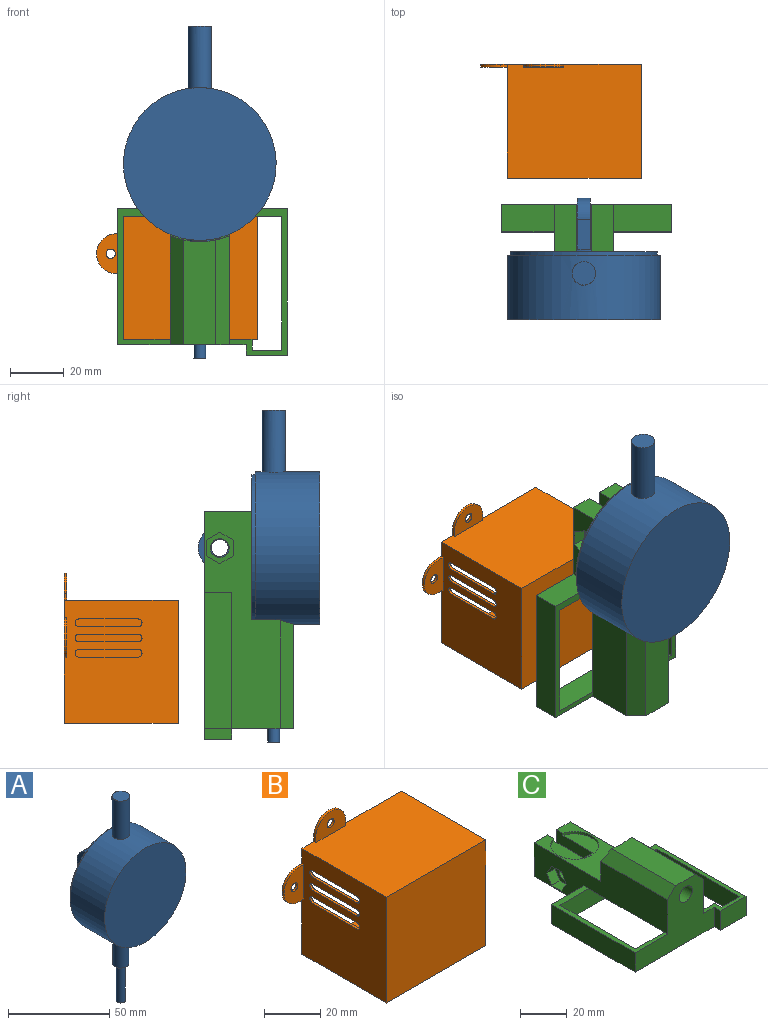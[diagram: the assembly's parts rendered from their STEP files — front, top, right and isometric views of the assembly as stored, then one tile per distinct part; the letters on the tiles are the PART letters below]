
ASSEMBLY  parts=3 mates=2
PART A: 31 faces, bbox 57x45.3x123.9 mm
  f0: cylinder r=28.5mm len=57mm, axis (0,1,0), area 4187.4mm2, adj f11,f12,f13,f15
  f1: plane 19x15.8mm, normal (1,0,0), area 242.2mm2, adj f3,f5,f6,f7,f8
  f2: plane 19x15.8mm, normal (-1,0,0), area 242.2mm2, adj f3,f5,f6,f7,f8
  f3: plane 20x20mm, normal (0,1,0), area 235.2mm2, adj f1,f2,f4,f5,f6
  f4: cylinder r=10mm len=20mm, axis (0,-1,0), area 62.8mm2, adj f3,f10
  f5: plane 11.1x5mm, normal (0,0,-1), area 55.5mm2, adj f1,f2,f3,f7
  f6: plane 11.1x5mm, normal (0,0,1), area 55.5mm2, adj f1,f2,f3,f7
  f7: cylinder r=7.9mm len=15.8mm, axis (1,0,0), area 124.1mm2, adj f1,f2,f5,f6
  f8: cylinder r=3.15mm len=6.3mm, axis (1,0,0), area 99mm2, adj f1,f2
  f9: cylinder r=27.4mm len=54.8mm, axis (0,1,0), area 223.8mm2, adj f10,f12
  f10: plane 54.8x54.8mm, normal (0,1,0), area 1980.8mm2, adj f4,f9,f21,f24,f27,f30
  f11: plane 57x57mm, normal (0,-1,0), area 2551.8mm2, adj f0
  f12: plane 57x57mm, normal (0,1,0), area 193.2mm2, adj f0,f9
  f13: cylinder r=4.35mm len=23.33mm, axis (0,0,-1), area 633.2mm2, adj f0,f14
  f14: plane 8.7x8.7mm, normal (0,0,1), area 59.4mm2, adj f13
  f15: cylinder r=4mm len=21.78mm, axis (0,0,1), area 543.9mm2, adj f0,f16
  f16: plane 8x8mm, normal (0,0,-1), area 35.1mm2, adj f15,f17
  f17: cylinder r=2.2mm len=22.4mm, axis (0,0,1), area 309.6mm2, adj f16,f18
  f18: plane 4.4x4.4mm, normal (0,0,-1), area 15.2mm2, adj f17
  f19: cone r=0mm half-angle=59deg, axis (0,1,0), area 3.7mm2, adj f20
  f20: cylinder r=1mm len=2mm, axis (0,1,0), area 4.7mm2, adj f19,f21
  f21: cone r=1mm half-angle=45deg, axis (0,1,0), area 18mm2, adj f10,f20
  f22: cone r=0mm half-angle=59deg, axis (0,1,0), area 3.7mm2, adj f23
  f23: cylinder r=1mm len=2mm, axis (0,1,0), area 4.7mm2, adj f22,f24
  f24: cone r=1mm half-angle=45deg, axis (0,1,0), area 18mm2, adj f10,f23
  f25: cone r=0mm half-angle=59deg, axis (0,1,0), area 3.7mm2, adj f26
  f26: cylinder r=1mm len=2mm, axis (0,1,0), area 4.7mm2, adj f25,f27
  f27: cone r=1mm half-angle=45deg, axis (0,1,0), area 18mm2, adj f10,f26
  f28: cone r=0mm half-angle=59deg, axis (0,1,0), area 3.7mm2, adj f29
  f29: cylinder r=1mm len=2mm, axis (0,1,0), area 4.7mm2, adj f28,f30
  f30: cone r=1mm half-angle=45deg, axis (0,1,0), area 18mm2, adj f10,f29
PART B: 33 faces, bbox 60x42.5x56 mm
  f0: plane 46x42.5mm, normal (-1,0,0), area 1735mm2, adj f1,f3,f4,f5,f11,f12,f15,f21
  f1: plane 50x42.5mm, normal (0,0,-1), area 2125mm2, adj f0,f2,f4,f5
  f2: plane 46x42.5mm, normal (1,0,0), area 1955mm2, adj f1,f3,f4,f5
  f3: plane 50x42.5mm, normal (0,0,1), area 2110mm2, adj f0,f2,f4,f5,f7,f9,f10
  f4: plane 50x46mm, normal (0,-1,0), area 2300mm2, adj f0,f1,f2,f3
  f5: plane 60x56mm, normal (0,1,0), area 420.5mm2, adj f0,f1,f2,f3,f6,f7,f8,f9
  f6: cylinder r=7.5mm len=15mm, axis (0,1,0), area 23.6mm2, adj f5,f7,f9,f10
  f7: plane 2.5x1mm, normal (-1,0,0), area 2.5mm2, adj f3,f5,f6,f10
  f8: cylinder r=1.75mm len=3.5mm, axis (0,1,0), area 11mm2, adj f5,f10
  f9: plane 2.5x1mm, normal (1,0,0), area 2.5mm2, adj f3,f5,f6,f10
  f10: plane 15x10mm, normal (0,-1,0), area 116.2mm2, adj f3,f6,f7,f8,f9
  f11: plane 2.5x1mm, normal (0,0,-1), area 2.5mm2, adj f0,f5,f13,f15
  f12: plane 2.5x1mm, normal (0,0,1), area 2.5mm2, adj f0,f5,f13,f15
  f13: cylinder r=7.5mm len=15mm, axis (0,1,0), area 23.6mm2, adj f5,f11,f12,f15
  f14: cylinder r=1.75mm len=3.5mm, axis (0,1,0), area 11mm2, adj f5,f15
  f15: plane 15x10mm, normal (0,-1,0), area 116.2mm2, adj f0,f11,f12,f13,f14
  f16: plane 44x41.5mm, normal (1,0,0), area 1621mm2, adj f5,f17,f19,f20,f21,f22,f23,f24
  f17: plane 48x41.5mm, normal (0,0,1), area 1992mm2, adj f5,f16,f18,f20
  f18: plane 44x41.5mm, normal (-1,0,0), area 1826mm2, adj f5,f17,f19,f20
  f19: plane 48x41.5mm, normal (0,0,-1), area 1992mm2, adj f5,f16,f18,f20
  f20: plane 48x44mm, normal (0,1,0), area 2112mm2, adj f16,f17,f18,f19
  f21: cylinder r=1.4mm len=2.8mm, axis (-1,0,0), area 4.4mm2, adj f0,f16,f22,f23
  f22: plane 22.2x1mm, normal (0,0,1), area 22.2mm2, adj f0,f16,f21,f24
  f23: plane 22.2x1mm, normal (0,0,-1), area 22.2mm2, adj f0,f16,f21,f24
  f24: cylinder r=1.4mm len=2.8mm, axis (-1,0,0), area 4.4mm2, adj f0,f16,f22,f23
  f25: cylinder r=1.4mm len=2.8mm, axis (-1,0,0), area 4.4mm2, adj f0,f16,f26,f27
  f26: plane 22.2x1mm, normal (0,0,1), area 22.2mm2, adj f0,f16,f25,f28
  f27: plane 22.2x1mm, normal (0,0,-1), area 22.2mm2, adj f0,f16,f25,f28
  f28: cylinder r=1.4mm len=2.8mm, axis (-1,0,0), area 4.4mm2, adj f0,f16,f26,f27
  f29: cylinder r=1.4mm len=2.8mm, axis (-1,0,0), area 4.4mm2, adj f0,f16,f30,f31
  f30: plane 22.2x1mm, normal (0,0,1), area 22.2mm2, adj f0,f16,f29,f32
  f31: plane 22.2x1mm, normal (0,0,-1), area 22.2mm2, adj f0,f16,f29,f32
  f32: cylinder r=1.4mm len=2.8mm, axis (-1,0,0), area 4.4mm2, adj f0,f16,f30,f31
PART C: 41 faces, bbox 63.4x85.1x33.2 mm
  f0: plane 16.46x5.5mm, normal (0,1,0), area 90.5mm2, adj f3,f4,f23,f37
  f1: plane 81.15x28.16mm, normal (1,0,0), area 1304.4mm2, adj f2,f8,f17,f22,f23,f24,f26,f34
  f2: plane 17.66x8.25mm, normal (0,1,0), area 145.7mm2, adj f1,f3,f23,f34
  f3: plane 22x17.66mm, normal (-1,0,0), area 328.2mm2, adj f0,f2,f23,f26,f34,f36,f37
  f4: plane 22x17.66mm, normal (1,0,0), area 328.2mm2, adj f0,f5,f7,f23,f34,f36,f37
  f5: plane 17.66x8.25mm, normal (0,1,0), area 145.7mm2, adj f4,f6,f23,f34
  f6: plane 81.15x28.16mm, normal (-1,0,0), area 1252.8mm2, adj f5,f9,f15,f17,f23,f24,f27,f28
  f7: cylinder r=3.5mm len=7mm, axis (-1,0,0), area 71.5mm2, adj f4,f33
  f8: plane 21.7x10.16mm, normal (0,1,0), area 220.4mm2, adj f1,f20,f22,f23
  f9: plane 50.8x19.7mm, normal (0,0,1), area 195.4mm2, adj f6,f10,f11,f12,f15,f16,f17
  f10: plane 48x10.16mm, normal (0,1,0), area 487.6mm2, adj f9,f11,f21,f22,f23,f24
  f11: plane 46x10.16mm, normal (1,0,0), area 467.3mm2, adj f9,f10,f12,f23
  f12: plane 59x10.16mm, normal (0,-1,0), area 599.3mm2, adj f9,f11,f13,f22,f23,f24
  f13: plane 50x10.16mm, normal (-1,0,0), area 507.9mm2, adj f12,f14,f22,f23
  f14: plane 11x10.16mm, normal (0,1,0), area 111.7mm2, adj f13,f21,f22,f23
  f15: plane 19.7x10.16mm, normal (0,1,0), area 200.1mm2, adj f6,f9,f16,f23
  f16: plane 50.8x10.16mm, normal (-1,0,0), area 516mm2, adj f9,f15,f17,f23
  f17: plane 48x33.16mm, normal (0,-1,0), area 918.3mm2, adj f1,f6,f9,f16,f18,f22,f23,f25
  f18: plane 10.16x4mm, normal (-1,0,0), area 40.6mm2, adj f17,f19,f22,f23
  f19: plane 15.39x10.16mm, normal (0,-1,0), area 156.3mm2, adj f18,f20,f22,f23
  f20: plane 54.8x10.16mm, normal (1,0,0), area 556.7mm2, adj f8,f19,f22,f23
  f21: plane 10.16x4mm, normal (1,0,0), area 40.6mm2, adj f10,f14,f22,f23
  f22: plane 54.8x21.7mm, normal (0,0,1), area 222.6mm2, adj f1,f8,f10,f12,f13,f14,f17,f18
  f23: plane 85.15x63.39mm, normal (0,0,-1), area 1070.2mm2, adj f0,f1,f2,f3,f4,f5,f6,f8
  f24: plane 46x22mm, normal (0,0,-1), area 1012.1mm2, adj f1,f6,f10,f12
  f25: plane 39.03x12mm, normal (0,0,1), area 463.3mm2, adj f17,f35,f39,f40
  f26: cylinder r=3.5mm len=8.25mm, axis (-1,0,0), area 181.4mm2, adj f1,f3
  f27: plane 5.1x5mm, normal (0,0.87,0.5), area 29.4mm2, adj f6,f28,f32,f33
  f28: plane 5.1x5mm, normal (0,0.87,-0.5), area 29.4mm2, adj f6,f27,f29,f33
  f29: plane 5.89x5mm, normal (0,0,-1), area 29.4mm2, adj f6,f28,f30,f33
  f30: plane 5.1x5mm, normal (0,-0.87,-0.5), area 29.4mm2, adj f6,f29,f31,f33
  f31: plane 5.1x5mm, normal (0,-0.87,0.5), area 29.4mm2, adj f6,f30,f32,f33
  f32: plane 5.89x5mm, normal (0,0,1), area 29.4mm2, adj f6,f27,f31,f33
  f33: plane 11.78x10.2mm, normal (-1,0,0), area 51.6mm2, adj f7,f27,f28,f29,f30,f31,f32
  f34: plane 42.75x22mm, normal (0,0,1), area 571.9mm2, adj f1,f2,f3,f4,f5,f6,f35,f36
  f35: cylinder r=29mm len=22mm, axis (0,0,-1), area 272.9mm2, adj f1,f6,f25,f34,f38,f39,f40
  f36: cylinder r=10.3mm len=20.6mm, axis (0,0,1), area 71mm2, adj f3,f4,f34,f37
  f37: plane 20.6x20.23mm, normal (0,0,1), area 231.9mm2, adj f0,f3,f4,f36
  f38: cylinder r=4mm len=38.68mm, axis (0,-1,0), area 968.6mm2, adj f17,f35
  f39: plane 40.57x5mm, normal (-0.71,0,0.71), area 280.8mm2, adj f6,f17,f25,f35
  f40: plane 40.57x5mm, normal (0.71,0,0.71), area 280.8mm2, adj f1,f17,f25,f35
PLACE A t=(28.5,-70,19.49)mm
PLACE B at identity
PLACE C rot(axis=(1,0,0),90deg) t=(29.5,-52.34,-23)mm
MATE slider C.f9 <-> B.f4  axis (0,-1,0) through (0,-62.5,0)mm
MATE slider C.f38 <-> A.f13  axis (0,0,-1) through (28.5,-78.15,-8.99)mm
